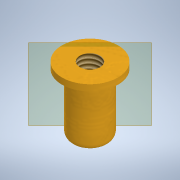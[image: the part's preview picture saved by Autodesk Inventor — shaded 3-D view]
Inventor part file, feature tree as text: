
AUTODESK INVENTOR PART (.ipt)
format: ipt  version: 2020.3 (Build 243373000, 373)  size: 130,560 bytes
history: native  units: mm
features: sketch x2, revolve x1, hole x1, fillet x1
ambient origin geometry x8: Origin, YZ Plane, XZ Plane, XY Plane, X Axis, Y Axis, Z Axis, Center Point
bodies: Solid1 (feature_tree)
feature tree (5):
  revolve  "Revolution1"  [1 undecoded]
  hole  "Hole1"  [1 undecoded]
  fillet  "Fillet1"  [1 undecoded]
  sketch  "Sketch1"  dims[d0=2.95mm d1=9.5mm]
  sketch  "Sketch2"  dims[d2=10.5mm d3=4.5mm d4=90.0deg d5=3.242mm d6=8.0mm d7=4.0mm d8=2.0mm d9=90.0deg d10=11.8mm d11=20.594885mm d12=1.0mm]
note: 3 required parameter values undecoded (feature->parameter linkage not recoverable at this tier; creation-order binding heuristic only, values carry confidence <= 0.55)